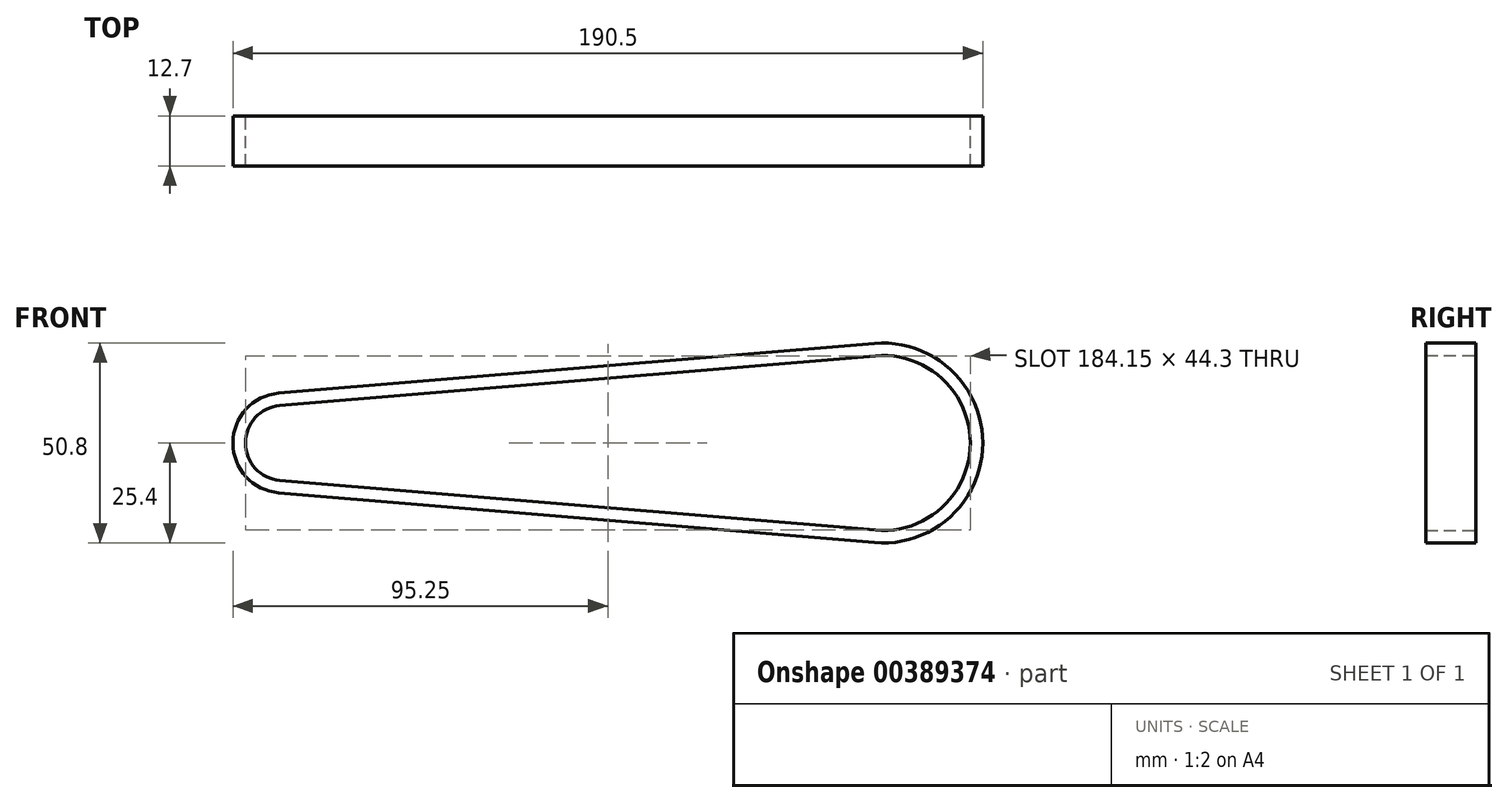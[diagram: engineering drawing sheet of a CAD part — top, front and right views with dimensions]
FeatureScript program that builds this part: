
annotation { "Feature Type Name" : "Feature", "Feature Type Description" : "" }
export const myFeature = defineFeature(function(context is Context, id is Id, definition is map)
    precondition{}
    {
        {
            var Q0;
            Q0=qCreatedBy(makeId("Front.planeOp"),FACE);
            var sketch = newSketch(context, id + "F0", { "sketchPlane" : qUnion([Q0])});
            skArc(sketch, "E0", {"start": v(-1.06, 12.66) * mm, "mid": v(-12.7, 0) * mm, "end": v(-1.06, -12.66) * mm});
            skArc(sketch, "E1", {"start": v(150.28, -25.31) * mm, "mid": v(177.8, 0) * mm, "end": v(150.28, 25.31) * mm});
            skLineSegment(sketch, "E2", {"start": v(-1.06, 12.66) * mm, "end": v(150.28, 25.31) * mm});
            skLineSegment(sketch, "E3", {"start": v(-1.06, -12.66) * mm, "end": v(150.28, -25.31) * mm});
            skArc(sketch, "E4", {"start": v(-0.8, 9.5) * mm, "mid": v(-9.53, 0) * mm, "end": v(-0.8, -9.5) * mm});
            skArc(sketch, "E5", {"start": v(150.55, -22.15) * mm, "mid": v(174.62, 0) * mm, "end": v(150.55, 22.15) * mm});
            skLineSegment(sketch, "E6", {"start": v(-0.8, -9.5) * mm, "end": v(150.55, -22.15) * mm});
            skLineSegment(sketch, "E7.trimOffspring", {"start": v(-0.8, 9.5) * mm, "end": v(150.55, 22.15) * mm});
            skSolve(sketch);
        }
        {
            var Q0;
            Q0 = qSketchRegion(id + "F0", true);
            extrude(context, id + "F1", {"entities" : qUnion([Q0]), "depth" : 12.7 * mm});
        }
    });
